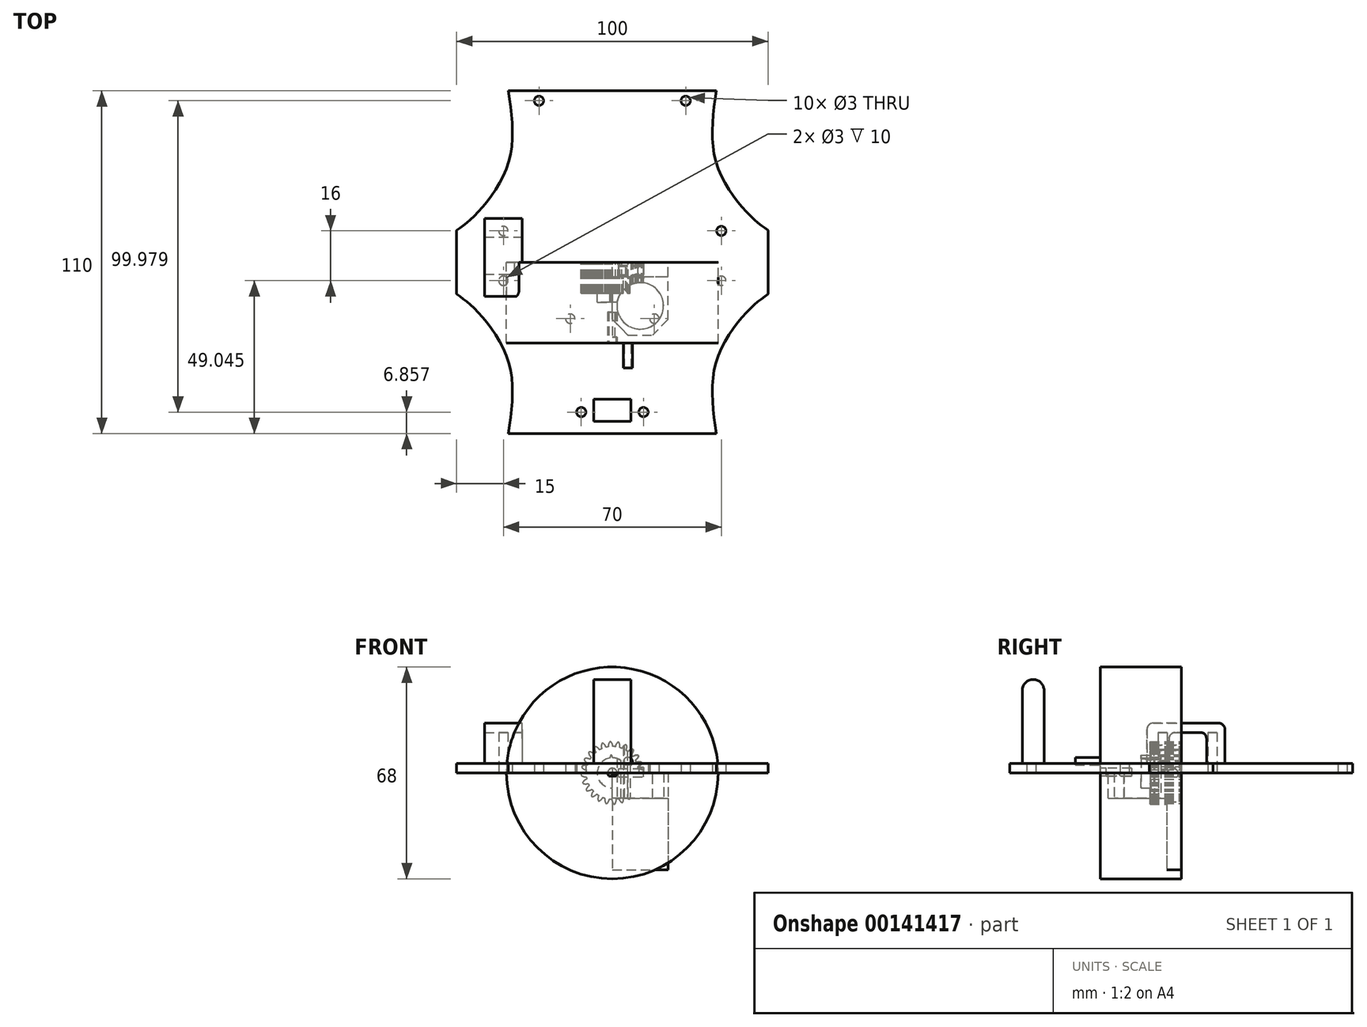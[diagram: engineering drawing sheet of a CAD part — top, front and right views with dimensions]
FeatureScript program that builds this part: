
annotation { "Feature Type Name" : "Feature", "Feature Type Description" : "" }
export const myFeature = defineFeature(function(context is Context, id is Id, definition is map)
    precondition{}
    {
        {
            var Q0;
            Q0=qCreatedBy(makeId("Front.planeOp"),FACE);
            var sketch = newSketch(context, id + "F0", { "sketchPlane" : qUnion([Q0])});
            skCircle(sketch, "E0", {"center": v(0, 0) * mm, "radius": 10 * mm, "construction": true});
            skCircle(sketch, "E1", {"center": v(0, 0) * mm, "radius": 9.24 * mm, "construction": true});
            skCircle(sketch, "E2", {"center": v(0, 0) * mm, "radius": 8.46 * mm});
            skLineSegment(sketch, "E3", {"start": v(0, 0) * mm, "end": v(0, 12.08) * mm, "construction": true});
            skLineSegment(sketch, "E4", {"start": v(0, 0) * mm, "end": v(-0.78, 11.94) * mm, "construction": true});
            skLineSegment(sketch, "E5", {"start": v(0, 9.24) * mm, "end": v(-6.89, 9.24) * mm, "construction": true});
            skLineSegment(sketch, "E6", {"start": v(0, 9.24) * mm, "end": v(-6.45, 6.9) * mm, "construction": true});
            skCircle(sketch, "E7", {"center": v(0, 9.24) * mm, "radius": 2.3 * mm, "construction": true});
            skCircle(sketch, "E8", {"center": v(0, 0) * mm, "radius": 8.68 * mm, "construction": true});
            skArc(sketch, "E9", {"start": v(0.15, 8.46) * mm, "mid": v(-0.02, 9.28) * mm, "end": v(-0.47, 9.99) * mm});
            skArc(sketch, "E10.MirrorCS", {"start": v(-1.26, 8.37) * mm, "mid": v(-1.2, 9.2) * mm, "end": v(-0.84, 9.97) * mm});
            skArc(sketch, "E11", {"start": v(-0.47, 9.99) * mm, "mid": v(-0.65, 9.99) * mm, "end": v(-0.84, 9.97) * mm});
            skArc(sketch, "E12.1.0", {"start": v(-2.04, 8.21) * mm, "mid": v(-2.42, 8.96) * mm, "end": v(-3.04, 9.53) * mm});
            skArc(sketch, "E12.1.1", {"start": v(-3.38, 7.76) * mm, "mid": v(-3.54, 8.58) * mm, "end": v(-3.39, 9.4) * mm});
            skArc(sketch, "E12.1.2", {"start": v(-3.04, 9.53) * mm, "mid": v(-3.22, 9.48) * mm, "end": v(-3.39, 9.4) * mm});
            skArc(sketch, "E12.2.0", {"start": v(-4.1, 7.4) * mm, "mid": v(-4.66, 8.03) * mm, "end": v(-5.4, 8.41) * mm});
            skArc(sketch, "E12.2.1", {"start": v(-5.27, 6.62) * mm, "mid": v(-5.64, 7.37) * mm, "end": v(-5.7, 8.21) * mm});
            skArc(sketch, "E12.2.2", {"start": v(-5.4, 8.41) * mm, "mid": v(-5.56, 8.32) * mm, "end": v(-5.7, 8.21) * mm});
            skArc(sketch, "E12.3.0", {"start": v(-5.87, 6.1) * mm, "mid": v(-6.58, 6.55) * mm, "end": v(-7.4, 6.73) * mm});
            skArc(sketch, "E12.3.1", {"start": v(-6.8, 5.03) * mm, "mid": v(-7.35, 5.66) * mm, "end": v(-7.64, 6.46) * mm});
            skArc(sketch, "E12.3.2", {"start": v(-7.4, 6.73) * mm, "mid": v(-7.53, 6.6) * mm, "end": v(-7.64, 6.46) * mm});
            skArc(sketch, "E12.4.0", {"start": v(-7.25, 4.36) * mm, "mid": v(-8.05, 4.63) * mm, "end": v(-8.89, 4.58) * mm});
            skArc(sketch, "E12.4.1", {"start": v(-7.87, 3.1) * mm, "mid": v(-8.57, 3.57) * mm, "end": v(-9.05, 4.26) * mm});
            skArc(sketch, "E12.4.2", {"start": v(-8.89, 4.58) * mm, "mid": v(-8.98, 4.43) * mm, "end": v(-9.05, 4.26) * mm});
            skArc(sketch, "E12.5.0", {"start": v(-8.13, 2.34) * mm, "mid": v(-8.97, 2.39) * mm, "end": v(-9.77, 2.13) * mm});
            skArc(sketch, "E12.5.1", {"start": v(-8.4, 0.95) * mm, "mid": v(-9.2, 1.23) * mm, "end": v(-9.84, 1.77) * mm});
            skArc(sketch, "E12.5.2", {"start": v(-9.77, 2.13) * mm, "mid": v(-9.82, 1.95) * mm, "end": v(-9.84, 1.77) * mm});
            skArc(sketch, "E12.6.0", {"start": v(-8.46, 0.15) * mm, "mid": v(-9.28, -0.02) * mm, "end": v(-9.99, -0.47) * mm});
            skArc(sketch, "E12.6.1", {"start": v(-8.37, -1.26) * mm, "mid": v(-9.2, -1.2) * mm, "end": v(-9.97, -0.84) * mm});
            skArc(sketch, "E12.6.2", {"start": v(-9.99, -0.47) * mm, "mid": v(-9.99, -0.65) * mm, "end": v(-9.97, -0.84) * mm});
            skArc(sketch, "E12.7.0", {"start": v(-8.21, -2.04) * mm, "mid": v(-8.96, -2.42) * mm, "end": v(-9.53, -3.04) * mm});
            skArc(sketch, "E12.7.1", {"start": v(-7.76, -3.38) * mm, "mid": v(-8.58, -3.54) * mm, "end": v(-9.4, -3.39) * mm});
            skArc(sketch, "E12.7.2", {"start": v(-9.53, -3.04) * mm, "mid": v(-9.48, -3.22) * mm, "end": v(-9.4, -3.39) * mm});
            skArc(sketch, "E12.8.0", {"start": v(-7.4, -4.1) * mm, "mid": v(-8.03, -4.66) * mm, "end": v(-8.41, -5.4) * mm});
            skArc(sketch, "E12.8.1", {"start": v(-6.62, -5.27) * mm, "mid": v(-7.37, -5.64) * mm, "end": v(-8.21, -5.7) * mm});
            skArc(sketch, "E12.8.2", {"start": v(-8.41, -5.4) * mm, "mid": v(-8.32, -5.56) * mm, "end": v(-8.21, -5.7) * mm});
            skArc(sketch, "E12.9.0", {"start": v(-6.1, -5.87) * mm, "mid": v(-6.55, -6.58) * mm, "end": v(-6.73, -7.4) * mm});
            skArc(sketch, "E12.9.1", {"start": v(-5.03, -6.8) * mm, "mid": v(-5.66, -7.35) * mm, "end": v(-6.46, -7.64) * mm});
            skArc(sketch, "E12.9.2", {"start": v(-6.73, -7.4) * mm, "mid": v(-6.6, -7.53) * mm, "end": v(-6.46, -7.64) * mm});
            skArc(sketch, "E12.10.0", {"start": v(-4.36, -7.25) * mm, "mid": v(-4.63, -8.05) * mm, "end": v(-4.58, -8.89) * mm});
            skArc(sketch, "E12.10.1", {"start": v(-3.1, -7.87) * mm, "mid": v(-3.57, -8.57) * mm, "end": v(-4.26, -9.05) * mm});
            skArc(sketch, "E12.10.2", {"start": v(-4.58, -8.89) * mm, "mid": v(-4.43, -8.98) * mm, "end": v(-4.26, -9.05) * mm});
            skArc(sketch, "E12.11.0", {"start": v(-2.34, -8.13) * mm, "mid": v(-2.39, -8.97) * mm, "end": v(-2.13, -9.77) * mm});
            skArc(sketch, "E12.11.1", {"start": v(-0.95, -8.4) * mm, "mid": v(-1.23, -9.2) * mm, "end": v(-1.77, -9.84) * mm});
            skArc(sketch, "E12.11.2", {"start": v(-2.13, -9.77) * mm, "mid": v(-1.95, -9.82) * mm, "end": v(-1.77, -9.84) * mm});
            skArc(sketch, "E12.12.0", {"start": v(-0.15, -8.46) * mm, "mid": v(0.02, -9.28) * mm, "end": v(0.47, -9.99) * mm});
            skArc(sketch, "E12.12.1", {"start": v(1.26, -8.37) * mm, "mid": v(1.2, -9.2) * mm, "end": v(0.84, -9.97) * mm});
            skArc(sketch, "E12.12.2", {"start": v(0.47, -9.99) * mm, "mid": v(0.65, -9.99) * mm, "end": v(0.84, -9.97) * mm});
            skArc(sketch, "E12.13.0", {"start": v(2.04, -8.21) * mm, "mid": v(2.42, -8.96) * mm, "end": v(3.04, -9.53) * mm});
            skArc(sketch, "E12.13.1", {"start": v(3.38, -7.76) * mm, "mid": v(3.54, -8.58) * mm, "end": v(3.39, -9.4) * mm});
            skArc(sketch, "E12.13.2", {"start": v(3.04, -9.53) * mm, "mid": v(3.22, -9.48) * mm, "end": v(3.39, -9.4) * mm});
            skArc(sketch, "E12.14.0", {"start": v(4.1, -7.4) * mm, "mid": v(4.66, -8.03) * mm, "end": v(5.4, -8.41) * mm});
            skArc(sketch, "E12.14.1", {"start": v(5.27, -6.62) * mm, "mid": v(5.64, -7.37) * mm, "end": v(5.7, -8.21) * mm});
            skArc(sketch, "E12.14.2", {"start": v(5.4, -8.41) * mm, "mid": v(5.56, -8.32) * mm, "end": v(5.7, -8.21) * mm});
            skArc(sketch, "E12.15.0", {"start": v(5.87, -6.1) * mm, "mid": v(6.58, -6.55) * mm, "end": v(7.4, -6.73) * mm});
            skArc(sketch, "E12.15.1", {"start": v(6.8, -5.03) * mm, "mid": v(7.35, -5.66) * mm, "end": v(7.64, -6.46) * mm});
            skArc(sketch, "E12.15.2", {"start": v(7.4, -6.73) * mm, "mid": v(7.53, -6.6) * mm, "end": v(7.64, -6.46) * mm});
            skArc(sketch, "E12.16.0", {"start": v(7.25, -4.36) * mm, "mid": v(8.05, -4.63) * mm, "end": v(8.89, -4.58) * mm});
            skArc(sketch, "E12.16.1", {"start": v(7.87, -3.1) * mm, "mid": v(8.57, -3.57) * mm, "end": v(9.05, -4.26) * mm});
            skArc(sketch, "E12.16.2", {"start": v(8.89, -4.58) * mm, "mid": v(8.98, -4.43) * mm, "end": v(9.05, -4.26) * mm});
            skArc(sketch, "E12.17.0", {"start": v(8.13, -2.34) * mm, "mid": v(8.97, -2.39) * mm, "end": v(9.77, -2.13) * mm});
            skArc(sketch, "E12.17.1", {"start": v(8.4, -0.95) * mm, "mid": v(9.2, -1.23) * mm, "end": v(9.84, -1.77) * mm});
            skArc(sketch, "E12.17.2", {"start": v(9.77, -2.13) * mm, "mid": v(9.82, -1.95) * mm, "end": v(9.84, -1.77) * mm});
            skArc(sketch, "E12.18.0", {"start": v(8.46, -0.15) * mm, "mid": v(9.28, 0.02) * mm, "end": v(9.99, 0.47) * mm});
            skArc(sketch, "E12.18.1", {"start": v(8.37, 1.26) * mm, "mid": v(9.2, 1.2) * mm, "end": v(9.97, 0.84) * mm});
            skArc(sketch, "E12.18.2", {"start": v(9.99, 0.47) * mm, "mid": v(9.99, 0.65) * mm, "end": v(9.97, 0.84) * mm});
            skArc(sketch, "E12.19.0", {"start": v(8.21, 2.04) * mm, "mid": v(8.96, 2.42) * mm, "end": v(9.53, 3.04) * mm});
            skArc(sketch, "E12.19.1", {"start": v(7.76, 3.38) * mm, "mid": v(8.58, 3.54) * mm, "end": v(9.4, 3.39) * mm});
            skArc(sketch, "E12.19.2", {"start": v(9.53, 3.04) * mm, "mid": v(9.48, 3.22) * mm, "end": v(9.4, 3.39) * mm});
            skArc(sketch, "E12.20.0", {"start": v(7.4, 4.1) * mm, "mid": v(8.03, 4.66) * mm, "end": v(8.41, 5.4) * mm});
            skArc(sketch, "E12.20.1", {"start": v(6.62, 5.27) * mm, "mid": v(7.37, 5.64) * mm, "end": v(8.21, 5.7) * mm});
            skArc(sketch, "E12.20.2", {"start": v(8.41, 5.4) * mm, "mid": v(8.32, 5.56) * mm, "end": v(8.21, 5.7) * mm});
            skArc(sketch, "E12.21.0", {"start": v(6.1, 5.87) * mm, "mid": v(6.55, 6.58) * mm, "end": v(6.73, 7.4) * mm});
            skArc(sketch, "E12.21.1", {"start": v(5.03, 6.8) * mm, "mid": v(5.66, 7.35) * mm, "end": v(6.46, 7.64) * mm});
            skArc(sketch, "E12.21.2", {"start": v(6.73, 7.4) * mm, "mid": v(6.6, 7.53) * mm, "end": v(6.46, 7.64) * mm});
            skArc(sketch, "E12.22.0", {"start": v(4.36, 7.25) * mm, "mid": v(4.63, 8.05) * mm, "end": v(4.58, 8.89) * mm});
            skArc(sketch, "E12.22.1", {"start": v(3.1, 7.87) * mm, "mid": v(3.57, 8.57) * mm, "end": v(4.26, 9.05) * mm});
            skArc(sketch, "E12.22.2", {"start": v(4.58, 8.89) * mm, "mid": v(4.43, 8.98) * mm, "end": v(4.26, 9.05) * mm});
            skArc(sketch, "E12.23.0", {"start": v(2.34, 8.13) * mm, "mid": v(2.39, 8.97) * mm, "end": v(2.13, 9.77) * mm});
            skArc(sketch, "E12.23.1", {"start": v(0.95, 8.4) * mm, "mid": v(1.23, 9.2) * mm, "end": v(1.77, 9.84) * mm});
            skArc(sketch, "E12.23.2", {"start": v(2.13, 9.77) * mm, "mid": v(1.95, 9.82) * mm, "end": v(1.77, 9.84) * mm});
            skCircle(sketch, "E13", {"center": v(-3.42, 7.98) * mm, "radius": 3.64 * mm, "construction": true});
            skSolve(sketch);
        }
        {
            var Q0;
            Q0 = qSketchRegion(id + "F0", true);
            extrude(context, id + "F1", {"entities" : qUnion([Q0]), "depth" : 10 * mm});
        }
        {
            var Q0;
            Q0=qCreatedBy(makeId("Front.planeOp"),FACE);
            var sketch = newSketch(context, id + "F2", { "sketchPlane" : qUnion([Q0])});
            skCircle(sketch, "E14", {"center": v(0, 0) * mm, "radius": 2.31 * mm, "construction": true});
            skCircle(sketch, "E15", {"center": v(0, 0) * mm, "radius": 2.12 * mm});
            skCircle(sketch, "E16", {"center": v(0, 0) * mm, "radius": 2.5 * mm, "construction": true});
            skLineSegment(sketch, "E17", {"start": v(0, 0) * mm, "end": v(0, 3.7) * mm, "construction": true});
            skLineSegment(sketch, "E18", {"start": v(0, 0) * mm, "end": v(-0.23, 3.58) * mm, "construction": true});
            skLineSegment(sketch, "E19", {"start": v(0, 2.31) * mm, "end": v(-2.42, 1.43) * mm, "construction": true});
            skLineSegment(sketch, "E20", {"start": v(0, 2.3) * mm, "end": v(-1.97, 2.3) * mm, "construction": true});
            skCircle(sketch, "E21", {"center": v(0, 0) * mm, "radius": 2.17 * mm, "construction": true});
            skCircle(sketch, "E22", {"center": v(-0.54, 2.1) * mm, "radius": 0.57 * mm, "construction": true});
            skArc(sketch, "E23", {"start": v(0.04, 2.11) * mm, "mid": v(0.03, 2.21) * mm, "end": v(0, 2.31) * mm});
            skArc(sketch, "E24", {"start": v(0, 2.3) * mm, "mid": v(-0.05, 2.4) * mm, "end": v(-0.12, 2.5) * mm});
            skArc(sketch, "E25.MirrorCS", {"start": v(-0.3, 2.3) * mm, "mid": v(-0.27, 2.4) * mm, "end": v(-0.21, 2.5) * mm});
            skArc(sketch, "E26.MirrorCS", {"start": v(-0.32, 2.1) * mm, "mid": v(-0.32, 2.2) * mm, "end": v(-0.3, 2.3) * mm});
            skArc(sketch, "E27", {"start": v(-0.12, 2.5) * mm, "mid": v(-0.16, 2.5) * mm, "end": v(-0.21, 2.5) * mm});
            skArc(sketch, "E28.1.0", {"start": v(-1.83, -1.4) * mm, "mid": v(-1.94, -1.43) * mm, "end": v(-2.05, -1.43) * mm});
            skArc(sketch, "E28.1.1", {"start": v(-1.65, -1.32) * mm, "mid": v(-1.74, -1.37) * mm, "end": v(-1.83, -1.4) * mm});
            skArc(sketch, "E28.1.2", {"start": v(-2.1, -1.35) * mm, "mid": v(-2.08, -1.4) * mm, "end": v(-2.05, -1.43) * mm});
            skArc(sketch, "E28.2.0", {"start": v(2.13, -0.88) * mm, "mid": v(2.2, -0.97) * mm, "end": v(2.26, -1.06) * mm});
            skArc(sketch, "E28.2.1", {"start": v(1.97, -0.77) * mm, "mid": v(2.06, -0.82) * mm, "end": v(2.13, -0.88) * mm});
            skArc(sketch, "E28.2.2", {"start": v(2.22, -1.15) * mm, "mid": v(2.25, -1.1) * mm, "end": v(2.26, -1.06) * mm});
            skCircle(sketch, "E29", {"center": v(0, 2.31) * mm, "radius": 0.57 * mm, "construction": true});
            skSolve(sketch);
        }
        {
            var Q0;
            Q0 = qSketchRegion(id + "F2", true);
            extrude(context, id + "F3", {"entities" : qUnion([Q0]), "depth" : 5.62 * mm});
        }
        {
            var Q0;
            Q0=makeQuery(id+"F3.opExtrude","SWEPT_BODY",BODY,{"disambiguationData":[OSD([sQuery(id+"F2.wireOp",EDGE,"E15"),sQuery(id+"F2.wireOp",EDGE,"E23"),sQuery(id+"F2.wireOp",EDGE,"E24"),sQuery(id+"F2.wireOp",EDGE,"E25.MirrorCS"),sQuery(id+"F2.wireOp",EDGE,"E26.MirrorCS"),sQuery(id+"F2.wireOp",EDGE,"E27")])]});
            var Q1;
            Q1=qCreatedBy(makeId("Origin.pointOp"),VERTEX);
            transform(context, id + "F4", {"entities" : qUnion([Q0]), "transformType" : TransformType.SCALE_UNIFORMLY, "scale" : 2.3, "scalePoint" : qUnion([Q1]), "makeCopy" : false});
        }
        {
            var Q0;
            Q0=qCreatedBy(makeId("Front.planeOp"),FACE);
            var sketch = newSketch(context, id + "F5", { "sketchPlane" : qUnion([Q0])});
            skLineSegment(sketch, "E30.bottom", {"start": v(0, 0) * mm, "end": v(17.91, 0) * mm});
            skLineSegment(sketch, "E30.top", {"start": v(0, -31.13) * mm, "end": v(17.91, -31.13) * mm});
            skLineSegment(sketch, "E30.left", {"start": v(0, 0) * mm, "end": v(0, -31.13) * mm});
            skLineSegment(sketch, "E30.right", {"start": v(17.91, 0) * mm, "end": v(17.91, -31.13) * mm});
            skSolve(sketch);
        }
        {
            var Q0;
            Q0 = qSketchRegion(id + "F5", true);
            extrude(context, id + "F6", {"entities" : qUnion([Q0]), "depth" : 4.6 * mm, "offsetDistance" : 25 * mm});
        }
        {
            var Q0;
            Q0=makeQuery(id+"F6.opExtrude","CAP_FACE",FACE,{"disambiguationData":[OSD([sQuery(id+"F5.wireOp",EDGE,"E30.bottom"),sQuery(id+"F5.wireOp",EDGE,"E30.top"),sQuery(id+"F5.wireOp",EDGE,"E30.left"),sQuery(id+"F5.wireOp",EDGE,"E30.right")])],"isStart":false});
            var sketch = newSketch(context, id + "F7", { "sketchPlane" : qUnion([Q0])});
            skLineSegment(sketch, "E31.bottom", {"start": v(0, 0) * mm, "end": v(17.91, 0) * mm});
            skLineSegment(sketch, "E31.top", {"start": v(0, -8.15) * mm, "end": v(17.91, -8.15) * mm});
            skLineSegment(sketch, "E31.left", {"start": v(0, 0) * mm, "end": v(0, -8.15) * mm});
            skLineSegment(sketch, "E31.right", {"start": v(17.91, 0) * mm, "end": v(17.91, -8.15) * mm});
            skSolve(sketch);
        }
        {
            var Q0;
            Q0 = qSketchRegion(id + "F7", true);
            extrude(context, id + "F8", {"entities" : qUnion([Q0]), "operationType" : NewBodyOperationType.ADD, "depth" : 18.8 * mm, "offsetDistance" : 25 * mm});
        }
        {
            var Q0;
            Q0=makeQuery(id+"F8.opExtrude","SWEPT_FACE",FACE,{"disambiguationData":[OSD([sQuery(id+"F7.wireOp",EDGE,"E31.top")])]});
            var sketch = newSketch(context, id + "F9", { "sketchPlane" : qUnion([Q0])});
            skLineSegment(sketch, "E32", {"start": v(0, 23.4) * mm, "end": v(17.91, 4.6) * mm});
            skLineSegment(sketch, "E33", {"start": v(17.91, 4.6) * mm, "end": v(17.91, 23.4) * mm});
            skLineSegment(sketch, "E34", {"start": v(17.91, 23.4) * mm, "end": v(0, 4.6) * mm});
            skCircle(sketch, "E35", {"center": v(8.96, 14) * mm, "radius": 7.48 * mm});
            skSolve(sketch);
        }
        {
            var Q0;
            {var subQ0=sQuery(id+"F9.wireOp",EDGE,"E35");var subQ1=sQuery(id+"F9.wireOp",EDGE,"E32");var subQ2=makeQuery(id+"F9.imprint","INTERSECT",VERTEX,{"disambiguationData":[OD(0.0)],"derivedFrom":[subQ1,subQ0]});Q0=makeQuery(id+"F9.imprint","IMPRINT",FACE,{"disambiguationData":[TD([[makeQuery(id+"F9.imprint","IMPRINT",EDGE,{"disambiguationData":[TD([[subQ2,-1.0]])],"derivedFrom":subQ1}),-1.0]])]});}
            var Q1;
            {var subQ0=sQuery(id+"F9.wireOp",EDGE,"E35");var subQ1=sQuery(id+"F9.wireOp",EDGE,"E32");var subQ2=makeQuery(id+"F9.imprint","INTERSECT",VERTEX,{"disambiguationData":[OD(0.0)],"derivedFrom":[subQ1,subQ0]});Q1=makeQuery(id+"F9.imprint","IMPRINT",FACE,{"disambiguationData":[TD([[makeQuery(id+"F9.imprint","IMPRINT",EDGE,{"disambiguationData":[TD([[subQ2,-1.0]])],"derivedFrom":subQ1}),1.0]])]});}
            var Q2;
            {var subQ0=sQuery(id+"F9.wireOp",EDGE,"E34");var subQ1=sQuery(id+"F9.wireOp",EDGE,"E32");var subQ2=makeQuery(id+"F9.imprint","INTERSECT",VERTEX,{"derivedFrom":[subQ1,subQ0]});Q2=makeQuery(id+"F9.imprint","IMPRINT",FACE,{"disambiguationData":[TD([[makeQuery(id+"F9.imprint","IMPRINT",EDGE,{"disambiguationData":[TD([[subQ2,-1.0]])],"derivedFrom":subQ1}),1.0]])]});}
            var Q3;
            {var subQ0=sQuery(id+"F9.wireOp",EDGE,"E34");var subQ1=sQuery(id+"F9.wireOp",EDGE,"E32");var subQ2=makeQuery(id+"F9.imprint","INTERSECT",VERTEX,{"derivedFrom":[subQ1,subQ0]});Q3=makeQuery(id+"F9.imprint","IMPRINT",FACE,{"disambiguationData":[TD([[makeQuery(id+"F9.imprint","IMPRINT",EDGE,{"disambiguationData":[TD([[subQ2,-1.0]])],"derivedFrom":subQ1}),-1.0]])]});}
            extrude(context, id + "F10", {"entities" : qUnion([Q0, Q1, Q2, Q3]), "operationType" : NewBodyOperationType.REMOVE, "oppositeDirection" : true, "depth" : 25 * mm, "offsetDistance" : 25 * mm});
        }
        {
            var Q0;
            Q0=makeQuery(id+"F8.opExtrude","CAP_EDGE",EDGE,{"disambiguationData":[OSD([sQuery(id+"F7.wireOp",EDGE,"E31.left")])],"isStart":false});
            var Q1;
            Q1=makeQuery(id+"F8.opExtrude","CAP_EDGE",EDGE,{"disambiguationData":[OSD([sQuery(id+"F7.wireOp",EDGE,"E31.right")])],"isStart":false});
            chamfer(context, id + "F11", {"entities" : qUnion([Q0, Q1]), "width" : 5 * mm, "tangentPropagation" : true});
        }
        {
            var Q0;
            Q0=qCreatedBy(makeId("Right.planeOp"),FACE);
            var sketch = newSketch(context, id + "F12", { "sketchPlane" : qUnion([Q0])});
            skLineSegment(sketch, "E36", {"start": v(0, 0) * mm, "end": v(-5.3, 0) * mm});
            skLineSegment(sketch, "E37", {"start": v(-2.65, 0) * mm, "end": v(-2.65, 1.75) * mm});
            skLineSegment(sketch, "E38", {"start": v(-2.65, 1.75) * mm, "end": v(-2.65, -1.75) * mm});
            skLineSegment(sketch, "E39", {"start": v(2.53, 1.75) * mm, "end": v(-9.07, 1.75) * mm});
            skLineSegment(sketch, "E40", {"start": v(-9.07, -1.75) * mm, "end": v(4.89, -1.75) * mm});
            skArc(sketch, "E41", {"start": v(-0.53, -1.75) * mm, "mid": v(0, 0) * mm, "end": v(-0.53, 1.75) * mm});
            skArc(sketch, "E42.MirrorCS", {"start": v(-4.77, -1.75) * mm, "mid": v(-5.3, 0) * mm, "end": v(-4.77, 1.75) * mm});
            skSolve(sketch);
        }
        {
            var Q0;
            {var subQ0=sQuery(id+"F12.wireOp",EDGE,"E37");Q0=makeQuery(id+"F12.imprint","IMPRINT",FACE,{"disambiguationData":[TD([[makeQuery(id+"F12.imprint","IMPRINT",EDGE,{"derivedFrom":subQ0}),-1.0]])]});}
            var Q1;
            {var subQ0=sQuery(id+"F12.wireOp",EDGE,"E37");Q1=makeQuery(id+"F12.imprint","IMPRINT",FACE,{"disambiguationData":[TD([[makeQuery(id+"F12.imprint","IMPRINT",EDGE,{"derivedFrom":subQ0}),1.0]])]});}
            var Q2;
            {var subQ0=sQuery(id+"F12.wireOp",EDGE,"E38");Q2=makeQuery(id+"F12.imprint","IMPRINT",FACE,{"disambiguationData":[TD([[makeQuery(id+"F12.imprint","IMPRINT",EDGE,{"derivedFrom":subQ0}),-1.0]])]});}
            var Q3;
            {var subQ0=sQuery(id+"F12.wireOp",EDGE,"E38");Q3=makeQuery(id+"F12.imprint","IMPRINT",FACE,{"disambiguationData":[TD([[makeQuery(id+"F12.imprint","IMPRINT",EDGE,{"derivedFrom":subQ0}),1.0]])]});}
            extrude(context, id + "F13", {"entities" : qUnion([Q0, Q1, Q2, Q3]), "depth" : 10 * mm, "offsetDistance" : 25 * mm});
        }
        {
            var Q0;
            Q0=makeQuery(id+"F13.opExtrude","CAP_FACE",FACE,{"disambiguationData":[OSD([sQuery(id+"F12.wireOp",EDGE,"E39"),sQuery(id+"F12.wireOp",EDGE,"E40"),sQuery(id+"F12.wireOp",EDGE,"E41"),sQuery(id+"F12.wireOp",EDGE,"E42.MirrorCS")])],"isStart":false});
            var sketch = newSketch(context, id + "F14", { "sketchPlane" : qUnion([Q0])});
            skLineSegment(sketch, "E43", {"start": v(-0.53, -1.75) * mm, "end": v(-0.53, 1.75) * mm});
            skArc(sketch, "E44", {"start": v(-1.27, -1.28) * mm, "mid": v(-2.65, 1.42) * mm, "end": v(-4.03, -1.28) * mm});
            skLineSegment(sketch, "E45", {"start": v(-2.65, -1.28) * mm, "end": v(-1.27, -1.28) * mm});
            skLineSegment(sketch, "E46", {"start": v(-1.27, -1.28) * mm, "end": v(-4.03, -1.28) * mm});
            skLineSegment(sketch, "E47", {"start": v(0, 0) * mm, "end": v(0, -5.33) * mm});
            skLineSegment(sketch, "E48", {"start": v(-3.2, -5.33) * mm, "end": v(0, -5.33) * mm});
            skSolve(sketch);
        }
        {
            var Q0;
            {var subQ0=sQuery(id+"F14.wireOp",EDGE,"E44");Q0=makeQuery(id+"F14.imprint","IMPRINT",FACE,{"disambiguationData":[TD([[makeQuery(id+"F14.imprint","IMPRINT",EDGE,{"derivedFrom":subQ0}),1.0]])]});}
            extrude(context, id + "F15", {"entities" : qUnion([Q0]), "operationType" : NewBodyOperationType.REMOVE, "oppositeDirection" : true, "depth" : 8 * mm, "offsetDistance" : 25 * mm});
        }
        {
            var Q0;
            Q0=makeQuery(id+"F13.opExtrude","CAP_FACE",FACE,{"disambiguationData":[OSD([sQuery(id+"F12.wireOp",EDGE,"E39"),sQuery(id+"F12.wireOp",EDGE,"E40"),sQuery(id+"F12.wireOp",EDGE,"E41"),sQuery(id+"F12.wireOp",EDGE,"E42.MirrorCS")])],"isStart":true});
            extrude(context, id + "F16", {"entities" : qUnion([Q0]), "operationType" : NewBodyOperationType.ADD, "depth" : 3 * mm, "offsetDistance" : 25 * mm});
        }
        {
            var Q0;
            Q0=qCreatedBy(makeId("Front.planeOp"),FACE);
            var sketch = newSketch(context, id + "F17", { "sketchPlane" : qUnion([Q0])});
            skCircle(sketch, "E49", {"center": v(0, 0) * mm, "radius": 34 * mm});
            skSolve(sketch);
        }
        {
            var Q0;
            Q0 = qSketchRegion(id + "F17", true);
            extrude(context, id + "F18", {"entities" : qUnion([Q0]), "depth" : 26 * mm, "offsetDistance" : 25 * mm});
        }
        {
            var Q0;
            Q0=makeQuery(id+"F18.opExtrude","CAP_FACE",FACE,{"disambiguationData":[OSD([sQuery(id+"F17.wireOp",EDGE,"E49")])],"isStart":false});
            var sketch = newSketch(context, id + "F19", { "sketchPlane" : qUnion([Q0])});
            skArc(sketch, "E50", {"start": v(1.12, -1) * mm, "mid": v(0, 1.5) * mm, "end": v(-1.12, -1) * mm});
            skLineSegment(sketch, "E51", {"start": v(0, 1.5) * mm, "end": v(0, -1) * mm});
            skLineSegment(sketch, "E52", {"start": v(-1.12, -1) * mm, "end": v(1.12, -1) * mm});
            skSolve(sketch);
        }
        {
            var Q0;
            Q0 = qSketchRegion(id + "F19", true);
            extrude(context, id + "F20", {"entities" : qUnion([Q0]), "operationType" : NewBodyOperationType.REMOVE, "oppositeDirection" : true, "depth" : 10 * mm, "offsetDistance" : 25 * mm});
        }
        {
            var Q0;
            Q0=qCreatedBy(makeId("Front.planeOp"),FACE);
            var sketch = newSketch(context, id + "F21", { "sketchPlane" : qUnion([Q0])});
            skLineSegment(sketch, "E53", {"start": v(0, 0) * mm, "end": v(0, 7) * mm});
            skLineSegment(sketch, "E54", {"start": v(10, 7) * mm, "end": v(10, 0) * mm});
            skArc(sketch, "E55", {"start": v(10, 7) * mm, "mid": v(5, 9.6) * mm, "end": v(0, 7) * mm});
            skArc(sketch, "E56", {"start": v(0, 0) * mm, "mid": v(5, -2.6) * mm, "end": v(10, 0) * mm});
            skLineSegment(sketch, "E57", {"start": v(0, 7) * mm, "end": v(10, 0) * mm});
            skLineSegment(sketch, "E58", {"start": v(0, 0) * mm, "end": v(10, 7) * mm});
            skSolve(sketch);
        }
        {
            var Q0;
            Q0 = qSketchRegion(id + "F21", true);
            extrude(context, id + "F22", {"entities" : qUnion([Q0]), "depth" : 24 * mm, "offsetDistance" : 25 * mm});
        }
        {
            var Q0;
            Q0=makeQuery(id+"F22.opExtrude","CAP_FACE",FACE,{"disambiguationData":[OSD([sQuery(id+"F21.wireOp",EDGE,"E53"),sQuery(id+"F21.wireOp",EDGE,"E54"),sQuery(id+"F21.wireOp",EDGE,"E55"),sQuery(id+"F21.wireOp",EDGE,"E56")])],"isStart":false});
            var sketch = newSketch(context, id + "F23", { "sketchPlane" : qUnion([Q0])});
            skArc(sketch, "E59", {"start": v(6.12, 2.5) * mm, "mid": v(5, 5) * mm, "end": v(3.88, 2.5) * mm});
            skLineSegment(sketch, "E60", {"start": v(5, 2.5) * mm, "end": v(6.12, 2.5) * mm});
            skLineSegment(sketch, "E61", {"start": v(6.12, 2.5) * mm, "end": v(3.88, 2.5) * mm});
            skSolve(sketch);
        }
        {
            var Q0;
            Q0 = qSketchRegion(id + "F23", true);
            extrude(context, id + "F24", {"entities" : qUnion([Q0]), "operationType" : NewBodyOperationType.ADD, "depth" : 10 * mm, "offsetDistance" : 25 * mm});
        }
        {
            var Q0;
            Q0=qCreatedBy(makeId("Top.planeOp"),FACE);
            var sketch = newSketch(context, id + "F25", { "sketchPlane" : qUnion([Q0])});
            skLineSegment(sketch, "E62.bottom", {"start": v(33.36, 55) * mm, "end": v(-33.36, 55) * mm});
            skLineSegment(sketch, "E62.top", {"start": v(33.36, -55) * mm, "end": v(-33.36, -55) * mm});
            skLineSegment(sketch, "E62.left", {"start": v(50, 10.27) * mm, "end": v(50, -10.27) * mm});
            skLineSegment(sketch, "E62.right", {"start": v(-50, 10.27) * mm, "end": v(-50, -10.27) * mm});
            skPoint(sketch, "E62.middle", {"position": v(0, 0) * mm});
            skCircle(sketch, "E63", {"center": v(-13.5, -18.14) * mm, "radius": 1.5 * mm});
            skCircle(sketch, "E64", {"center": v(13.5, -18.14) * mm, "radius": 1.5 * mm});
            skLineSegment(sketch, "E65.bottom", {"start": v(-26.5, 4.36) * mm, "end": v(26.5, 4.36) * mm});
            skLineSegment(sketch, "E65.top", {"start": v(-26.5, -53.14) * mm, "end": v(26.5, -53.14) * mm});
            skLineSegment(sketch, "E65.left", {"start": v(-26.5, 4.36) * mm, "end": v(-26.5, -53.14) * mm});
            skLineSegment(sketch, "E65.right", {"start": v(26.5, 4.36) * mm, "end": v(26.5, -53.14) * mm});
            skLineSegment(sketch, "E66.bottom", {"start": v(26.5, -53.14) * mm, "end": v(-26.5, -53.14) * mm});
            skLineSegment(sketch, "E66.top", {"start": v(26.5, 14.86) * mm, "end": v(-26.5, 14.86) * mm});
            skLineSegment(sketch, "E66.left", {"start": v(26.5, -53.14) * mm, "end": v(26.5, 14.86) * mm});
            skLineSegment(sketch, "E66.right", {"start": v(-26.5, -53.14) * mm, "end": v(-26.5, 14.86) * mm});
            skPoint(sketch, "E66.middle", {"position": v(0, -19.14) * mm});
            skCircle(sketch, "E67", {"center": v(35, 10.04) * mm, "radius": 1.5 * mm});
            skCircle(sketch, "E68", {"center": v(35, -5.96) * mm, "radius": 1.5 * mm});
            skCircle(sketch, "E69.MirrorC", {"center": v(-35, 10.04) * mm, "radius": 1.5 * mm});
            skCircle(sketch, "E70.MirrorC", {"center": v(-35, -5.96) * mm, "radius": 1.5 * mm});
            skFitSpline(sketch, "E71", {"points": [v(-33.36, -55) * mm, v(-33.36, -31.94) * mm, v(-43.92, -15.27) * mm, v(-50, -10.27) * mm], "startDerivative": vector(8.25, 59.38) * mm, "endDerivative": vector(-24.16, 17.14) * mm});
            skFitSpline(sketch, "E72.MirrorCS", {"points": [v(-33.36, 55) * mm, v(-33.36, 31.94) * mm, v(-43.92, 15.27) * mm, v(-50, 10.27) * mm], "startDerivative": vector(8.25, -59.38) * mm, "endDerivative": vector(-24.16, -17.14) * mm});
            skFitSpline(sketch, "E73.MirrorCS", {"points": [v(33.36, 55) * mm, v(33.36, 31.94) * mm, v(43.92, 15.27) * mm, v(50, 10.27) * mm], "startDerivative": vector(-8.25, -59.38) * mm, "endDerivative": vector(24.16, -17.14) * mm});
            skFitSpline(sketch, "E74.MirrorCS", {"points": [v(33.36, -55) * mm, v(33.36, -31.94) * mm, v(43.92, -15.27) * mm, v(50, -10.27) * mm], "startDerivative": vector(-8.25, 59.38) * mm, "endDerivative": vector(24.16, 17.14) * mm});
            skPoint(sketch, "E75.orphan", {"position": v(50, 55) * mm});
            skPoint(sketch, "E76.orphan", {"position": v(50, -55) * mm});
            skPoint(sketch, "E77.orphan", {"position": v(-50, -55) * mm});
            skPoint(sketch, "E78.orphan", {"position": v(-50, 55) * mm});
            skCircle(sketch, "E79", {"center": v(-23.56, 51.84) * mm, "radius": 1.5 * mm});
            skCircle(sketch, "E80.MirrorC", {"center": v(23.56, 51.84) * mm, "radius": 1.5 * mm});
            skCircle(sketch, "E81", {"center": v(10, -48.14) * mm, "radius": 1.5 * mm});
            skCircle(sketch, "E82", {"center": v(-10, -48.14) * mm, "radius": 1.5 * mm});
            skSolve(sketch);
        }
        {
            var Q0;
            Q0=makeQuery(id+"F25.imprint","IMPRINT",FACE,{"disambiguationData":[TD([[makeQuery(id+"F25.imprint","IMPRINT",EDGE,{"derivedFrom":sQuery(id+"F25.wireOp",EDGE,"E62.bottom")}),1.0]])]});
            var Q1;
            Q1=makeQuery(id+"F25.imprint","IMPRINT",FACE,{"disambiguationData":[TD([[makeQuery(id+"F25.imprint","IMPRINT",EDGE,{"derivedFrom":sQuery(id+"F25.wireOp",EDGE,"E63")}),-1.0]])]});
            var Q2;
            Q2=makeQuery(id+"F25.imprint","IMPRINT",FACE,{"disambiguationData":[TD([[makeQuery(id+"F25.imprint","IMPRINT",EDGE,{"derivedFrom":sQuery(id+"F25.wireOp",EDGE,"E65.bottom")}),1.0]])]});
            extrude(context, id + "F26", {"entities" : qUnion([Q0, Q1, Q2]), "depth" : 3 * mm, "offsetDistance" : 25 * mm});
        }
        {
            var Q0;
            Q0=makeQuery(id+"F26.opExtrude","CAP_FACE",FACE,{"disambiguationData":[OSD([sQuery(id+"F25.wireOp",EDGE,"E62.bottom"),sQuery(id+"F25.wireOp",EDGE,"E62.top"),sQuery(id+"F25.wireOp",EDGE,"E62.left"),sQuery(id+"F25.wireOp",EDGE,"E62.right"),sQuery(id+"F25.wireOp",EDGE,"E63"),sQuery(id+"F25.wireOp",EDGE,"E64"),sQuery(id+"F25.wireOp",EDGE,"E67"),sQuery(id+"F25.wireOp",EDGE,"E68"),sQuery(id+"F25.wireOp",EDGE,"E69.MirrorC"),sQuery(id+"F25.wireOp",EDGE,"E70.MirrorC"),sQuery(id+"F25.wireOp",EDGE,"E71"),sQuery(id+"F25.wireOp",EDGE,"E72.MirrorCS"),sQuery(id+"F25.wireOp",EDGE,"E73.MirrorCS"),sQuery(id+"F25.wireOp",EDGE,"E74.MirrorCS"),sQuery(id+"F25.wireOp",EDGE,"E79"),sQuery(id+"F25.wireOp",EDGE,"E80.MirrorC"),sQuery(id+"F25.wireOp",EDGE,"E81"),sQuery(id+"F25.wireOp",EDGE,"E82")])],"isStart":false});
            var sketch = newSketch(context, id + "F27", { "sketchPlane" : qUnion([Q0])});
            skLineSegment(sketch, "E83.bottom", {"start": v(-41, 14.03) * mm, "end": v(-29, 14.03) * mm});
            skLineSegment(sketch, "E83.top", {"start": v(-41, -10.97) * mm, "end": v(-29, -10.97) * mm});
            skLineSegment(sketch, "E83.left", {"start": v(-41, 14.03) * mm, "end": v(-41, -10.97) * mm});
            skLineSegment(sketch, "E83.right", {"start": v(-29, 14.03) * mm, "end": v(-29, -10.97) * mm});
            skCircle(sketch, "E84", {"center": v(-35, 10.04) * mm, "radius": 1.5 * mm});
            skCircle(sketch, "E85", {"center": v(-35, -5.96) * mm, "radius": 1.5 * mm});
            skLineSegment(sketch, "E86.bottom", {"start": v(-41, 8.13) * mm, "end": v(-29, 8.13) * mm});
            skLineSegment(sketch, "E86.top", {"start": v(-41, -3.87) * mm, "end": v(-29, -3.87) * mm});
            skLineSegment(sketch, "E86.left", {"start": v(-41, 8.13) * mm, "end": v(-41, -3.87) * mm});
            skLineSegment(sketch, "E86.right", {"start": v(-29, 8.13) * mm, "end": v(-29, -3.87) * mm});
            skSolve(sketch);
        }
        {
            var Q0;
            {var subQ1=sQuery(id+"F27.wireOp",EDGE,"E83.bottom");Q0=makeQuery(id+"F27.imprint","IMPRINT",FACE,{"disambiguationData":[TD([[makeQuery(id+"F27.imprint","IMPRINT",EDGE,{"derivedFrom":subQ1}),-1.0]])]});}
            var Q1;
            {var subQ1=sQuery(id+"F27.wireOp",EDGE,"E83.top");Q1=makeQuery(id+"F27.imprint","IMPRINT",FACE,{"disambiguationData":[TD([[makeQuery(id+"F27.imprint","IMPRINT",EDGE,{"derivedFrom":subQ1}),1.0]])]});}
            extrude(context, id + "F28", {"entities" : qUnion([Q0, Q1]), "depth" : 10 * mm, "offsetDistance" : 25 * mm});
        }
        {
            var Q0;
            Q0=makeQuery(id+"F28.opExtrude","CAP_FACE",FACE,{"disambiguationData":[OSD([sQuery(id+"F27.wireOp",EDGE,"E83.bottom"),sQuery(id+"F27.wireOp",EDGE,"E83.left"),sQuery(id+"F27.wireOp",EDGE,"E83.right"),sQuery(id+"F27.wireOp",EDGE,"E84"),sQuery(id+"F27.wireOp",EDGE,"E86.bottom")])],"isStart":false});
            var sketch = newSketch(context, id + "F29", { "sketchPlane" : qUnion([Q0])});
            skLineSegment(sketch, "E87.bottom", {"start": v(-41, 14.03) * mm, "end": v(-29, 14.03) * mm});
            skLineSegment(sketch, "E87.top", {"start": v(-41, -10.97) * mm, "end": v(-29, -10.97) * mm});
            skLineSegment(sketch, "E87.left", {"start": v(-41, 14.03) * mm, "end": v(-41, -10.97) * mm});
            skLineSegment(sketch, "E87.right", {"start": v(-29, 14.03) * mm, "end": v(-29, -10.97) * mm});
            skSolve(sketch);
        }
        {
            var Q0;
            Q0 = qSketchRegion(id + "F29", true);
            extrude(context, id + "F30", {"entities" : qUnion([Q0]), "operationType" : NewBodyOperationType.ADD, "depth" : 3 * mm, "offsetDistance" : 25 * mm});
        }
        {
            var Q0;
            Q0=makeQuery(id+"F28.opExtrude","CAP_EDGE",EDGE,{"disambiguationData":[OSD([sQuery(id+"F27.wireOp",EDGE,"E86.bottom")])],"isStart":false});
            var Q1;
            Q1=makeQuery(id+"F28.opExtrude","CAP_EDGE",EDGE,{"disambiguationData":[OSD([sQuery(id+"F27.wireOp",EDGE,"E86.top")])],"isStart":false});
            var Q2;
            Q2=makeQuery(id+"F30.opExtrude","CAP_EDGE",EDGE,{"disambiguationData":[OSD([sQuery(id+"F29.wireOp",EDGE,"E87.top")])],"isStart":false});
            var Q3;
            Q3=makeQuery(id+"F30.opExtrude","CAP_EDGE",EDGE,{"disambiguationData":[OSD([sQuery(id+"F29.wireOp",EDGE,"E87.bottom")])],"isStart":false});
            fillet(context, id + "F31", {"entities" : qUnion([Q0, Q1, Q2, Q3]), "radius" : 2 * mm, "tangentPropagation" : true, "allowEdgeOverflow" : false});
        }
        {
            var Q0;
            Q0=makeQuery(id+"F26.opExtrude","CAP_FACE",FACE,{"disambiguationData":[OSD([sQuery(id+"F25.wireOp",EDGE,"E62.bottom"),sQuery(id+"F25.wireOp",EDGE,"E62.top"),sQuery(id+"F25.wireOp",EDGE,"E62.left"),sQuery(id+"F25.wireOp",EDGE,"E62.right"),sQuery(id+"F25.wireOp",EDGE,"E63"),sQuery(id+"F25.wireOp",EDGE,"E64"),sQuery(id+"F25.wireOp",EDGE,"E67"),sQuery(id+"F25.wireOp",EDGE,"E68"),sQuery(id+"F25.wireOp",EDGE,"E69.MirrorC"),sQuery(id+"F25.wireOp",EDGE,"E70.MirrorC"),sQuery(id+"F25.wireOp",EDGE,"E71"),sQuery(id+"F25.wireOp",EDGE,"E72.MirrorCS"),sQuery(id+"F25.wireOp",EDGE,"E73.MirrorCS"),sQuery(id+"F25.wireOp",EDGE,"E74.MirrorCS"),sQuery(id+"F25.wireOp",EDGE,"E79"),sQuery(id+"F25.wireOp",EDGE,"E80.MirrorC"),sQuery(id+"F25.wireOp",EDGE,"E81"),sQuery(id+"F25.wireOp",EDGE,"E82")])],"isStart":false});
            var sketch = newSketch(context, id + "F32", { "sketchPlane" : qUnion([Q0])});
            skLineSegment(sketch, "E88.bottom", {"start": v(-6, -51.05) * mm, "end": v(6, -51.05) * mm});
            skLineSegment(sketch, "E88.top", {"start": v(-6, -44.05) * mm, "end": v(6, -44.05) * mm});
            skLineSegment(sketch, "E88.left", {"start": v(-6, -51.05) * mm, "end": v(-6, -44.05) * mm});
            skLineSegment(sketch, "E88.right", {"start": v(6, -51.05) * mm, "end": v(6, -44.05) * mm});
            skSolve(sketch);
        }
        {
            var Q0;
            Q0 = qSketchRegion(id + "F32", true);
            extrude(context, id + "F33", {"entities" : qUnion([Q0]), "operationType" : NewBodyOperationType.ADD, "depth" : 27 * mm, "offsetDistance" : 25 * mm});
        }
        {
            var Q0;
            Q0=makeQuery(id+"F33.opExtrude","CAP_EDGE",EDGE,{"disambiguationData":[OSD([sQuery(id+"F32.wireOp",EDGE,"E88.top")])],"isStart":false});
            var Q1;
            Q1=makeQuery(id+"F33.opExtrude","CAP_EDGE",EDGE,{"disambiguationData":[OSD([sQuery(id+"F32.wireOp",EDGE,"E88.bottom")])],"isStart":false});
            fillet(context, id + "F34", {"entities" : qUnion([Q0, Q1]), "radius" : 3.5 * mm, "tangentPropagation" : true, "allowEdgeOverflow" : false});
        }
    });
